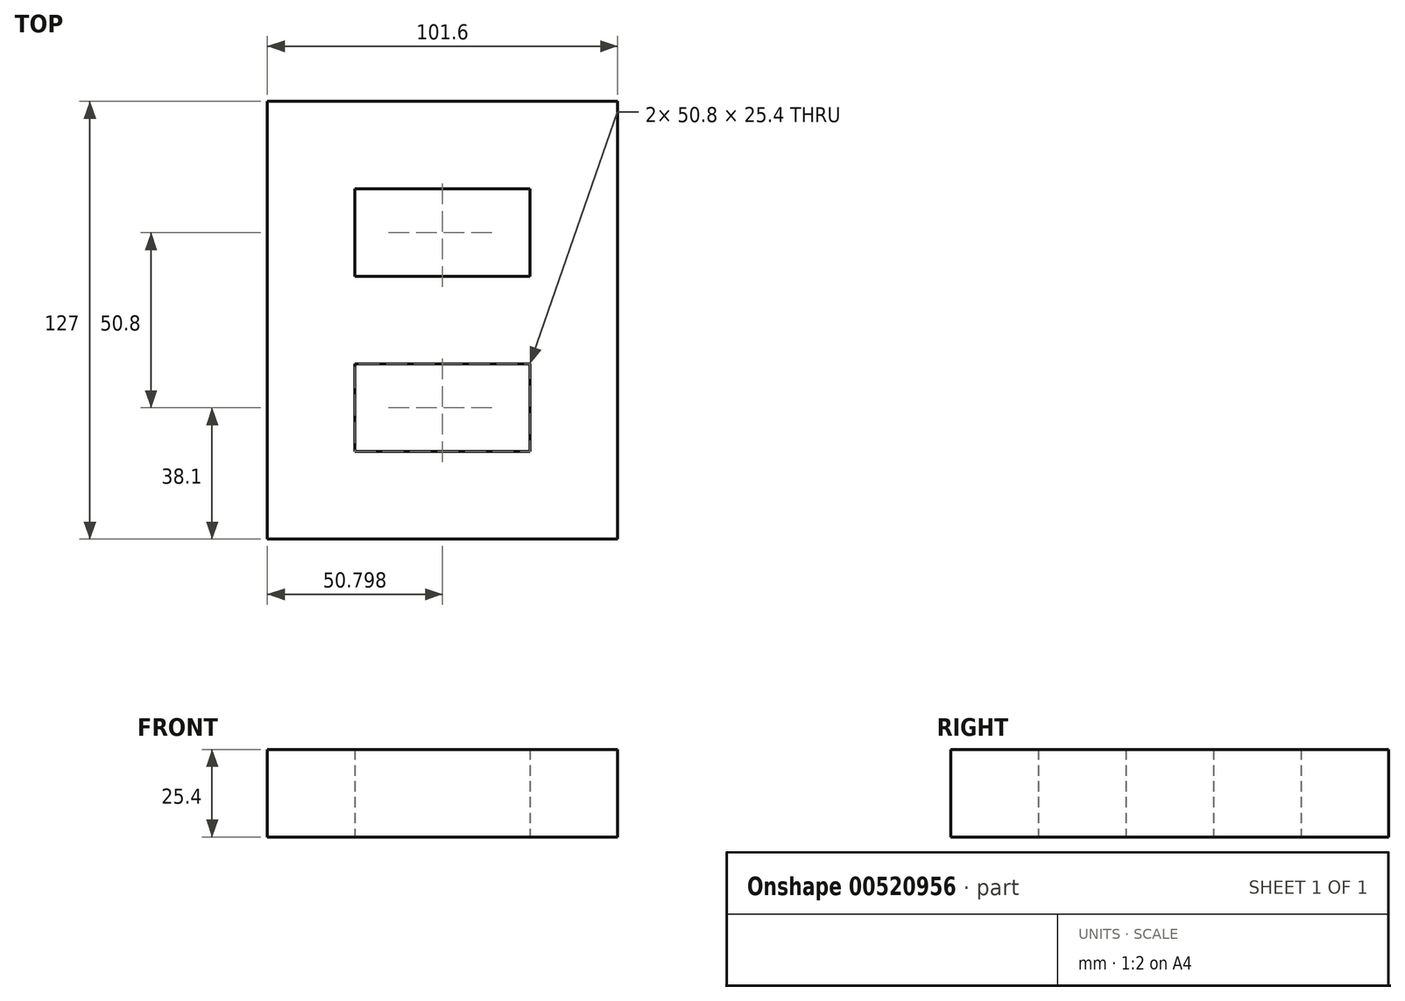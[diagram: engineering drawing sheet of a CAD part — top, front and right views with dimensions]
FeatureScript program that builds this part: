
annotation { "Feature Type Name" : "Feature", "Feature Type Description" : "" }
export const myFeature = defineFeature(function(context is Context, id is Id, definition is map)
    precondition{}
    {
        {
            var Q0;
            Q0=qCreatedBy(makeId("Top.planeOp"),FACE);
            var sketch = newSketch(context, id + "F0", { "sketchPlane" : qUnion([Q0])});
            skLineSegment(sketch, "E0", {"start": v(-53.13, 75.59) * mm, "end": v(48.47, 75.59) * mm});
            skLineSegment(sketch, "E1", {"start": v(-53.13, 75.59) * mm, "end": v(-53.13, -51.41) * mm});
            skLineSegment(sketch, "E2", {"start": v(-53.13, -51.41) * mm, "end": v(48.47, -51.41) * mm});
            skLineSegment(sketch, "E3", {"start": v(-27.73, -0.61) * mm, "end": v(23.07, -0.61) * mm});
            skLineSegment(sketch, "E4", {"start": v(-27.73, -0.61) * mm, "end": v(-27.73, -26.01) * mm});
            skLineSegment(sketch, "E5", {"start": v(23.07, -0.61) * mm, "end": v(23.07, -26.01) * mm});
            skLineSegment(sketch, "E6", {"start": v(-27.73, -26.01) * mm, "end": v(23.07, -26.01) * mm});
            skLineSegment(sketch, "E7", {"start": v(-27.73, 24.79) * mm, "end": v(-27.73, 50.19) * mm});
            skLineSegment(sketch, "E8", {"start": v(-27.73, 50.19) * mm, "end": v(23.07, 50.19) * mm});
            skLineSegment(sketch, "E9", {"start": v(-27.73, 24.79) * mm, "end": v(23.07, 24.79) * mm});
            skLineSegment(sketch, "E10", {"start": v(23.07, 24.79) * mm, "end": v(23.07, 50.19) * mm});
            skLineSegment(sketch, "E11", {"start": v(48.47, 75.59) * mm, "end": v(48.47, -51.41) * mm});
            skSolve(sketch);
        }
        {
            var Q0;
            Q0=makeQuery(id+"F0.imprint","IMPRINT",FACE,{"disambiguationData":[TD([[makeQuery(id+"F0.imprint","IMPRINT",EDGE,{"derivedFrom":sQuery(id+"F0.wireOp",EDGE,"E0")}),-1.0]])]});
            extrude(context, id + "F1", {"entities" : qUnion([Q0]), "depth" : 25.4 * mm, "offsetDistance" : 25.4 * mm});
        }
    });
